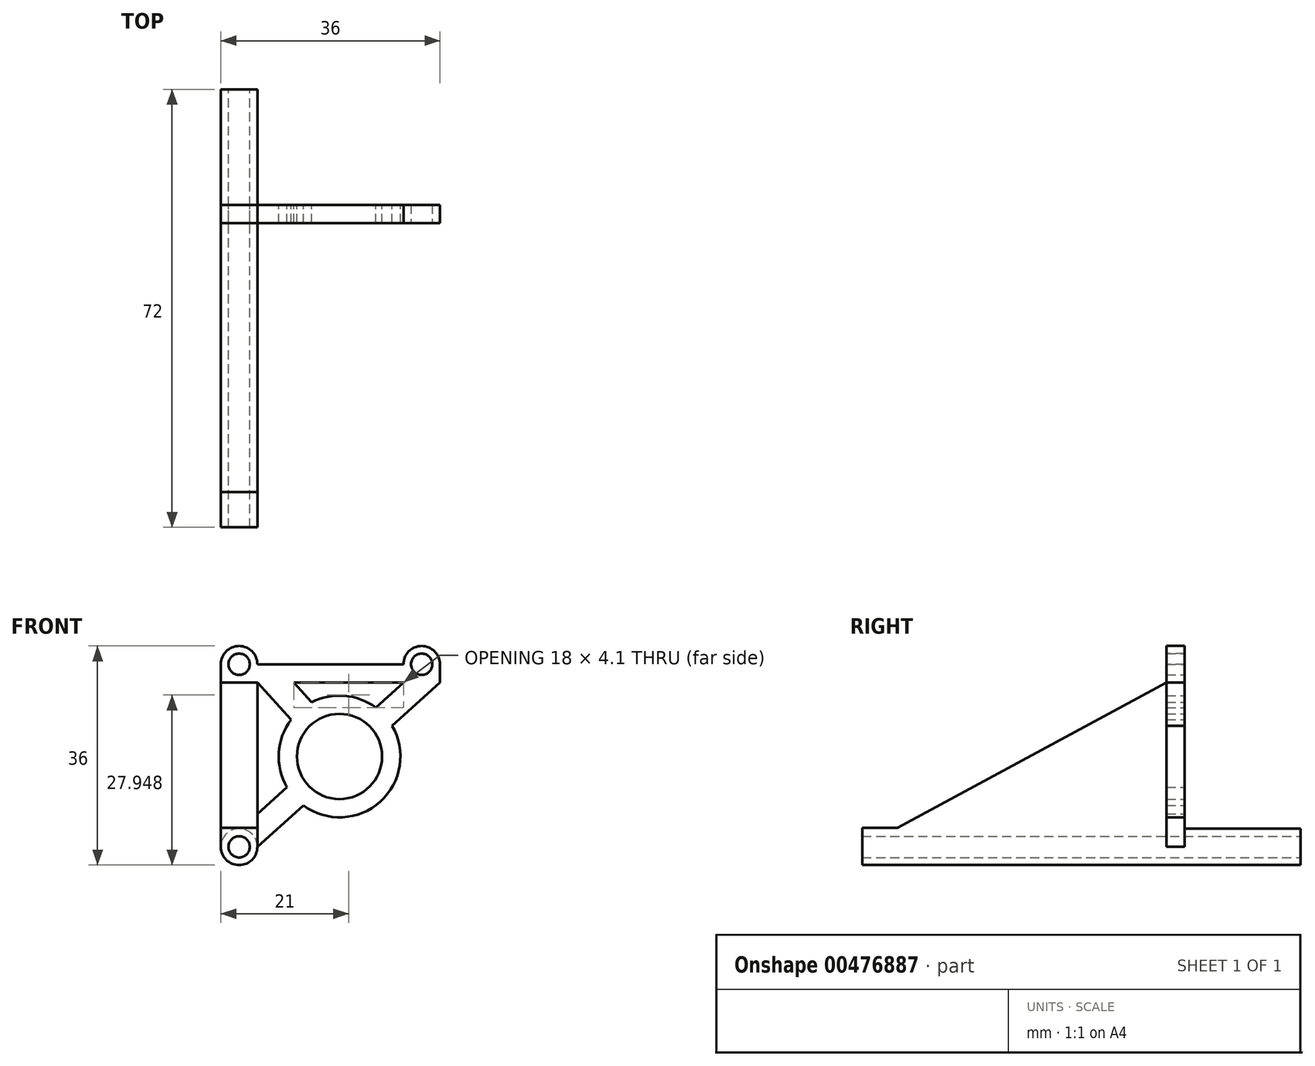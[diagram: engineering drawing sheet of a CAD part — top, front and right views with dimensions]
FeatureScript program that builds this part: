
annotation { "Feature Type Name" : "Feature", "Feature Type Description" : "" }
export const myFeature = defineFeature(function(context is Context, id is Id, definition is map)
    precondition{}
    {
        {
            var Q0;
            Q0=qCreatedBy(makeId("Front.planeOp"),FACE);
            var sketch = newSketch(context, id + "F0", { "sketchPlane" : qUnion([Q0])});
            skCircle(sketch, "E0", {"center": v(0, 0) * mm, "radius": 1.75 * mm});
            skCircle(sketch, "E1", {"center": v(0, 0) * mm, "radius": 3 * mm});
            skSolve(sketch);
        }
        {
            var Q0;
            Q0 = qSketchRegion(id + "F0", true);
            extrude(context, id + "F1", {"entities" : qUnion([Q0]), "depth" : 16 * mm, "hasSecondDirection" : true, "secondDirectionOppositeDirection" : true, "secondDirectionDepth" : 3 * mm});
        }
        {
            var Q0;
            Q0=makeQuery(id+"F1.opExtrude","CAP_FACE",FACE,{"disambiguationData":[OSD([sQuery(id+"F0.wireOp",EDGE,"E0"),sQuery(id+"F0.wireOp",EDGE,"E1")])],"isStart":false});
            var sketch = newSketch(context, id + "F2", { "sketchPlane" : qUnion([Q0])});
            skLineSegment(sketch, "E2", {"start": v(-3, 0) * mm, "end": v(-3, 30) * mm});
            skLineSegment(sketch, "E3", {"start": v(3, 0) * mm, "end": v(3, 30) * mm});
            skArc(sketch, "E4", {"start": v(-3, 0) * mm, "mid": v(0, -3) * mm, "end": v(3, 0) * mm});
            skArc(sketch, "E5", {"start": v(3, 30) * mm, "mid": v(0, 33) * mm, "end": v(-3, 30) * mm});
            skLineSegment(sketch, "E6", {"start": v(-3, 30) * mm, "end": v(3, 30) * mm, "construction": true});
            skCircle(sketch, "E7", {"center": v(0, 30) * mm, "radius": 1.75 * mm});
            skSolve(sketch);
        }
        {
            var Q0;
            Q0 = qSketchRegion(id + "F2", true);
            extrude(context, id + "F3", {"entities" : qUnion([Q0]), "operationType" : NewBodyOperationType.ADD, "depth" : 3 * mm});
        }
        {
            var Q0;
            Q0=makeQuery(id+"F3.opExtrude","SWEPT_FACE",FACE,{"disambiguationData":[OSD([sQuery(id+"F2.wireOp",EDGE,"E2")])]});
            var sketch = newSketch(context, id + "F4", { "sketchPlane" : qUnion([Q0])});
            skLineSegment(sketch, "E8", {"start": v(19, 27) * mm, "end": v(69, 0) * mm});
            skLineSegment(sketch, "E9", {"start": v(69, 0) * mm, "end": v(19, 0) * mm});
            skSolve(sketch);
        }
        {
            var Q0;
            {var subQ0=sQuery(id+"F4.wireOp",EDGE,"E8");Q0=makeQuery(id+"F4.imprint","IMPRINT",FACE,{"disambiguationData":[TD([[makeQuery(id+"F4.imprint","IMPRINT",EDGE,{"derivedFrom":subQ0}),-1.0]])]});}
            var Q1;
            Q1=makeQuery(id+"F3.opExtrude","SWEPT_FACE",FACE,{"disambiguationData":[OSD([sQuery(id+"F2.wireOp",EDGE,"E3")])]});
            extrude(context, id + "F5", {"entities" : qUnion([Q0]), "operationType" : NewBodyOperationType.ADD, "endBound" : BoundingType.UP_TO_SURFACE, "oppositeDirection" : true, "endBoundEntityFace" : qUnion([Q1]), "depth" : 5 * mm});
        }
        {
            var Q0;
            {var subQ0=sQuery(id+"F2.wireOp",EDGE,"E4");var subQ1=sQuery(id+"F2.wireOp",EDGE,"E3");var subQ2=sQuery(id+"F2.wireOp",EDGE,"E2");Q0=makeQuery(id+"F5.boolean.opBoolean","SPLIT",FACE,{"disambiguationData":[TD([makeQuery(id+"F1.opExtrude","SWEPT_FACE",FACE,{"disambiguationData":[OSD([sQuery(id+"F0.wireOp",EDGE,"E1")])]})])],"derivedFrom":makeQuery(id+"F3.opExtrude","CAP_FACE",FACE,{"disambiguationData":[OSD([subQ2,subQ1,subQ0,sQuery(id+"F2.wireOp",EDGE,"E5"),sQuery(id+"F2.wireOp",EDGE,"E7")])],"isStart":false})});}
            var sketch = newSketch(context, id + "F6", { "sketchPlane" : qUnion([Q0])});
            skArc(sketch, "E10", {"start": v(-3, 0) * mm, "mid": v(0, -3) * mm, "end": v(3, 0) * mm});
            skLineSegment(sketch, "E11", {"start": v(-3, 0) * mm, "end": v(3, 0) * mm});
            skSolve(sketch);
        }
        {
            var Q0;
            Q0 = qSketchRegion(id + "F6", true);
            var Q1;
            Q1=makeQuery(id+"F5.opExtrude","CAP_VERTEX",VERTEX,{"disambiguationData":[OSD([sQuery(id+"F4.wireOp",EDGE,"E8"),sQuery(id+"F4.wireOp",EDGE,"E9")])],"isStart":true});
            extrude(context, id + "F7", {"entities" : qUnion([Q0]), "operationType" : NewBodyOperationType.ADD, "endBound" : BoundingType.UP_TO_VERTEX, "endBoundEntityVertex" : qUnion([Q1]), "depth" : 25.4 * mm});
        }
        {
            var Q0;
            Q0=makeQuery(id+"F1.opExtrude","CAP_FACE",FACE,{"disambiguationData":[OSD([sQuery(id+"F0.wireOp",EDGE,"E0"),sQuery(id+"F0.wireOp",EDGE,"E1")])],"isStart":true});
            var sketch = newSketch(context, id + "F8", { "sketchPlane" : qUnion([Q0])});
            skCircle(sketch, "E12", {"center": v(0, 0) * mm, "radius": 1.75 * mm});
            skSolve(sketch);
        }
        {
            var Q0;
            Q0=makeQuery(id+"F7.opExtrude","CAP_FACE",FACE,{"disambiguationData":[OSD([sQuery(id+"F6.wireOp",EDGE,"E10"),sQuery(id+"F6.wireOp",EDGE,"E11")])],"isStart":false});
            var sketch = newSketch(context, id + "F9", { "sketchPlane" : qUnion([Q0])});
            skArc(sketch, "E13", {"start": v(-3, 0) * mm, "mid": v(0, -3) * mm, "end": v(3, 0) * mm});
            skLineSegment(sketch, "E14.top", {"start": v(-3, 3.13) * mm, "end": v(3, 3.13) * mm});
            skLineSegment(sketch, "E14.left", {"start": v(-3, 0) * mm, "end": v(-3, 3.13) * mm});
            skLineSegment(sketch, "E14.right", {"start": v(3, 0) * mm, "end": v(3, 3.13) * mm});
            skSolve(sketch);
        }
        {
            var Q0;
            Q0 = qSketchRegion(id + "F9", true);
            extrude(context, id + "F10", {"entities" : qUnion([Q0]), "operationType" : NewBodyOperationType.ADD, "oppositeDirection" : true, "depth" : 6 * mm});
        }
        {
            var Q0;
            Q0 = qSketchRegion(id + "F8", true);
            extrude(context, id + "F11", {"entities" : qUnion([Q0]), "operationType" : NewBodyOperationType.REMOVE, "endBound" : BoundingType.THROUGH_ALL, "oppositeDirection" : true, "depth" : 25.4 * mm});
        }
        {
            var Q0;
            {var subQ0=sQuery(id+"F2.wireOp",EDGE,"E7");var subQ3=sQuery(id+"F2.wireOp",EDGE,"E2");var subQ4=sQuery(id+"F2.wireOp",EDGE,"E3");var subQ5=sQuery(id+"F2.wireOp",EDGE,"E5");Q0=makeQuery(id+"F5.boolean.opBoolean","SPLIT",FACE,{"disambiguationData":[TD([makeQuery(id+"F3.opExtrude","SWEPT_FACE",FACE,{"disambiguationData":[OSD([subQ5])]})])],"derivedFrom":makeQuery(id+"F3.opExtrude","CAP_FACE",FACE,{"disambiguationData":[OSD([subQ3,subQ4,sQuery(id+"F2.wireOp",EDGE,"E4"),subQ5,subQ0])],"isStart":false})});}
            var sketch = newSketch(context, id + "F12", { "sketchPlane" : qUnion([Q0])});
            skCircle(sketch, "E15", {"center": v(30, 30) * mm, "radius": 1.75 * mm});
            skLineSegment(sketch, "E16", {"start": v(0, 30) * mm, "end": v(30, 30) * mm, "construction": true});
            skArc(sketch, "E17", {"start": v(33, 30) * mm, "mid": v(30, 33) * mm, "end": v(27, 30) * mm});
            skLineSegment(sketch, "E18", {"start": v(27, 30) * mm, "end": v(27, 27) * mm});
            skLineSegment(sketch, "E19", {"start": v(27, 27) * mm, "end": v(33, 27) * mm});
            skLineSegment(sketch, "E20", {"start": v(33, 27) * mm, "end": v(33, 30) * mm});
            skSolve(sketch);
        }
        {
            var Q0;
            Q0 = qSketchRegion(id + "F12", true);
            extrude(context, id + "F13", {"entities" : qUnion([Q0]), "oppositeDirection" : true, "depth" : 3 * mm});
        }
        {
            var Q0;
            Q0=makeQuery(id+"F10.boolean.opBoolean","MERGE",FACE,{"derivedFrom":[makeQuery(id+"F5.boolean.opBoolean","MERGE",FACE,{"derivedFrom":[makeQuery(id+"F3.opExtrude","SWEPT_FACE",FACE,{"disambiguationData":[OSD([sQuery(id+"F2.wireOp",EDGE,"E3")])]}),makeQuery(id+"F5.opExtrude","CAP_FACE",FACE,{"disambiguationData":[OSD([sQuery(id+"F2.wireOp",EDGE,"E2"),sQuery(id+"F4.wireOp",EDGE,"E8"),sQuery(id+"F4.wireOp",EDGE,"E9")])],"isStart":false})]}),makeQuery(id+"F10.opExtrude","SWEPT_FACE",FACE,{"disambiguationData":[OSD([sQuery(id+"F9.wireOp",EDGE,"E14.right")])]})]});
            var sketch = newSketch(context, id + "F14", { "sketchPlane" : qUnion([Q0])});
            skLineSegment(sketch, "E21.bottom", {"start": v(-19, 30) * mm, "end": v(-16, 30) * mm});
            skLineSegment(sketch, "E21.top", {"start": v(-19, 27) * mm, "end": v(-16, 27) * mm});
            skLineSegment(sketch, "E21.left", {"start": v(-19, 30) * mm, "end": v(-19, 27) * mm});
            skLineSegment(sketch, "E21.right", {"start": v(-16, 30) * mm, "end": v(-16, 27) * mm});
            skSolve(sketch);
        }
        {
            var Q0;
            Q0 = qSketchRegion(id + "F14", true);
            var Q1;
            Q1=makeQuery(id+"F13.opExtrude","SWEPT_FACE",FACE,{"disambiguationData":[OSD([sQuery(id+"F12.wireOp",EDGE,"E18")])]});
            extrude(context, id + "F15", {"entities" : qUnion([Q0]), "operationType" : NewBodyOperationType.ADD, "endBound" : BoundingType.UP_TO_SURFACE, "endBoundEntityFace" : qUnion([Q1]), "depth" : 25.4 * mm});
        }
        {
            var Q0;
            {var subQ0=sQuery(id+"F2.wireOp",EDGE,"E4");var subQ1=sQuery(id+"F2.wireOp",EDGE,"E3");var subQ2=sQuery(id+"F2.wireOp",EDGE,"E2");var subQ3=sQuery(id+"F2.wireOp",EDGE,"E5");var subQ4=sQuery(id+"F2.wireOp",EDGE,"E7");Q0=makeQuery(id+"F15.boolean.opBoolean","MERGE",FACE,{"derivedFrom":[makeQuery(id+"F3.boolean.opBoolean","SPLIT",FACE,{"disambiguationData":[TD([makeQuery(id+"F1.opExtrude","SWEPT_FACE",FACE,{"disambiguationData":[OSD([sQuery(id+"F0.wireOp",EDGE,"E1")])]})])],"derivedFrom":makeQuery(id+"F3.opExtrude","CAP_FACE",FACE,{"disambiguationData":[OSD([subQ2,subQ1,subQ0,subQ3,subQ4])],"isStart":true})}),makeQuery(id+"F15.opExtrude","SWEPT_FACE",FACE,{"disambiguationData":[OSD([sQuery(id+"F14.wireOp",EDGE,"E21.right")])]})]});}
            var sketch = newSketch(context, id + "F16", { "sketchPlane" : qUnion([Q0])});
            skLineSegment(sketch, "E22", {"start": v(-33, 27) * mm, "end": v(-3, 0) * mm});
            skLineSegment(sketch, "E23", {"start": v(-27, 27) * mm, "end": v(-3, 5.4) * mm});
            skLineSegment(sketch, "E24", {"start": v(-33, 27) * mm, "end": v(-27, 27) * mm});
            skLineSegment(sketch, "E25", {"start": v(-3, 5.4) * mm, "end": v(-3, 0) * mm});
            skSolve(sketch);
        }
        {
            var Q0;
            Q0 = qSketchRegion(id + "F16", true);
            var Q1;
            {var subQ0=sQuery(id+"F2.wireOp",EDGE,"E7");var subQ3=sQuery(id+"F2.wireOp",EDGE,"E2");var subQ4=sQuery(id+"F2.wireOp",EDGE,"E3");var subQ5=sQuery(id+"F2.wireOp",EDGE,"E5");Q1=makeQuery(id+"F15.boolean.opBoolean","MERGE",FACE,{"derivedFrom":[makeQuery(id+"F5.boolean.opBoolean","SPLIT",FACE,{"disambiguationData":[TD([makeQuery(id+"F3.opExtrude","SWEPT_FACE",FACE,{"disambiguationData":[OSD([subQ5])]})])],"derivedFrom":makeQuery(id+"F3.opExtrude","CAP_FACE",FACE,{"disambiguationData":[OSD([subQ3,subQ4,sQuery(id+"F2.wireOp",EDGE,"E4"),subQ5,subQ0])],"isStart":false})}),makeQuery(id+"F13.opExtrude","CAP_FACE",FACE,{"disambiguationData":[OSD([sQuery(id+"F12.wireOp",EDGE,"E15"),sQuery(id+"F12.wireOp",EDGE,"E17"),sQuery(id+"F12.wireOp",EDGE,"E18"),sQuery(id+"F12.wireOp",EDGE,"E19"),sQuery(id+"F12.wireOp",EDGE,"E20")])],"isStart":true}),makeQuery(id+"F15.opExtrude","SWEPT_FACE",FACE,{"disambiguationData":[OSD([sQuery(id+"F14.wireOp",EDGE,"E21.left")])]})]});}
            extrude(context, id + "F17", {"entities" : qUnion([Q0]), "operationType" : NewBodyOperationType.ADD, "endBound" : BoundingType.UP_TO_SURFACE, "oppositeDirection" : true, "endBoundEntityFace" : qUnion([Q1]), "depth" : 25.4 * mm});
        }
        {
            var Q0;
            {var subQ0=sQuery(id+"F2.wireOp",EDGE,"E4");var subQ1=sQuery(id+"F2.wireOp",EDGE,"E3");var subQ2=sQuery(id+"F2.wireOp",EDGE,"E2");var subQ3=sQuery(id+"F2.wireOp",EDGE,"E5");var subQ4=sQuery(id+"F2.wireOp",EDGE,"E7");Q0=makeQuery(id+"F17.boolean.opBoolean","MERGE",FACE,{"derivedFrom":[makeQuery(id+"F15.boolean.opBoolean","MERGE",FACE,{"derivedFrom":[makeQuery(id+"F3.boolean.opBoolean","SPLIT",FACE,{"disambiguationData":[TD([makeQuery(id+"F1.opExtrude","SWEPT_FACE",FACE,{"disambiguationData":[OSD([sQuery(id+"F0.wireOp",EDGE,"E1")])]})])],"derivedFrom":makeQuery(id+"F3.opExtrude","CAP_FACE",FACE,{"disambiguationData":[OSD([subQ2,subQ1,subQ0,subQ3,subQ4])],"isStart":true})}),makeQuery(id+"F15.opExtrude","SWEPT_FACE",FACE,{"disambiguationData":[OSD([sQuery(id+"F14.wireOp",EDGE,"E21.right")])]})]}),makeQuery(id+"F17.opExtrude","CAP_FACE",FACE,{"disambiguationData":[OSD([sQuery(id+"F16.wireOp",EDGE,"E22"),sQuery(id+"F16.wireOp",EDGE,"E23"),sQuery(id+"F16.wireOp",EDGE,"E24"),sQuery(id+"F16.wireOp",EDGE,"E25")])],"isStart":true})]});}
            var sketch = newSketch(context, id + "F18", { "sketchPlane" : qUnion([Q0])});
            skCircle(sketch, "E26", {"center": v(-16.5, 14.85) * mm, "radius": 10 * mm});
            skLineSegment(sketch, "E27", {"start": v(-30, 27) * mm, "end": v(-3, 2.7) * mm, "construction": true});
            skLineSegment(sketch, "E28", {"start": v(-33, 27) * mm, "end": v(-27, 27) * mm, "construction": true});
            skLineSegment(sketch, "E29", {"start": v(-3, 5.4) * mm, "end": v(-3, 0) * mm, "construction": true});
            skCircle(sketch, "E30", {"center": v(-16.5, 14.85) * mm, "radius": 7 * mm});
            skSolve(sketch);
        }
        {
            var Q0;
            Q0 = qSketchRegion(id + "F18", true);
            var Q1;
            {var subQ0=sQuery(id+"F2.wireOp",EDGE,"E7");var subQ3=sQuery(id+"F2.wireOp",EDGE,"E2");var subQ4=sQuery(id+"F2.wireOp",EDGE,"E3");var subQ5=sQuery(id+"F2.wireOp",EDGE,"E5");Q1=makeQuery(id+"F17.boolean.opBoolean","MERGE",FACE,{"derivedFrom":[makeQuery(id+"F15.boolean.opBoolean","MERGE",FACE,{"derivedFrom":[makeQuery(id+"F5.boolean.opBoolean","SPLIT",FACE,{"disambiguationData":[TD([makeQuery(id+"F3.opExtrude","SWEPT_FACE",FACE,{"disambiguationData":[OSD([subQ5])]})])],"derivedFrom":makeQuery(id+"F3.opExtrude","CAP_FACE",FACE,{"disambiguationData":[OSD([subQ3,subQ4,sQuery(id+"F2.wireOp",EDGE,"E4"),subQ5,subQ0])],"isStart":false})}),makeQuery(id+"F13.opExtrude","CAP_FACE",FACE,{"disambiguationData":[OSD([sQuery(id+"F12.wireOp",EDGE,"E15"),sQuery(id+"F12.wireOp",EDGE,"E17"),sQuery(id+"F12.wireOp",EDGE,"E18"),sQuery(id+"F12.wireOp",EDGE,"E19"),sQuery(id+"F12.wireOp",EDGE,"E20")])],"isStart":true}),makeQuery(id+"F15.opExtrude","SWEPT_FACE",FACE,{"disambiguationData":[OSD([sQuery(id+"F14.wireOp",EDGE,"E21.left")])]})]}),makeQuery(id+"F17.opExtrude","CAP_FACE",FACE,{"disambiguationData":[OSD([sQuery(id+"F16.wireOp",EDGE,"E22"),sQuery(id+"F16.wireOp",EDGE,"E23"),sQuery(id+"F16.wireOp",EDGE,"E24"),sQuery(id+"F16.wireOp",EDGE,"E25")])],"isStart":false})]});}
            extrude(context, id + "F19", {"entities" : qUnion([Q0]), "operationType" : NewBodyOperationType.ADD, "endBound" : BoundingType.UP_TO_SURFACE, "oppositeDirection" : true, "endBoundEntityFace" : qUnion([Q1]), "depth" : 25.4 * mm});
        }
        {
            var Q0;
            {var subQ0=sQuery(id+"F2.wireOp",EDGE,"E4");var subQ1=sQuery(id+"F2.wireOp",EDGE,"E3");var subQ2=sQuery(id+"F2.wireOp",EDGE,"E2");var subQ3=sQuery(id+"F2.wireOp",EDGE,"E5");var subQ4=sQuery(id+"F2.wireOp",EDGE,"E7");Q0=makeQuery(id+"F19.boolean.opBoolean","MERGE",FACE,{"derivedFrom":[makeQuery(id+"F17.boolean.opBoolean","MERGE",FACE,{"derivedFrom":[makeQuery(id+"F15.boolean.opBoolean","MERGE",FACE,{"derivedFrom":[makeQuery(id+"F3.boolean.opBoolean","SPLIT",FACE,{"disambiguationData":[TD([makeQuery(id+"F1.opExtrude","SWEPT_FACE",FACE,{"disambiguationData":[OSD([sQuery(id+"F0.wireOp",EDGE,"E1")])]})])],"derivedFrom":makeQuery(id+"F3.opExtrude","CAP_FACE",FACE,{"disambiguationData":[OSD([subQ2,subQ1,subQ0,subQ3,subQ4])],"isStart":true})}),makeQuery(id+"F15.opExtrude","SWEPT_FACE",FACE,{"disambiguationData":[OSD([sQuery(id+"F14.wireOp",EDGE,"E21.right")])]})]}),makeQuery(id+"F17.opExtrude","CAP_FACE",FACE,{"disambiguationData":[OSD([sQuery(id+"F16.wireOp",EDGE,"E22"),sQuery(id+"F16.wireOp",EDGE,"E23"),sQuery(id+"F16.wireOp",EDGE,"E24"),sQuery(id+"F16.wireOp",EDGE,"E25")])],"isStart":true})]}),makeQuery(id+"F19.opExtrude","CAP_FACE",FACE,{"disambiguationData":[OSD([sQuery(id+"F18.wireOp",EDGE,"E26"),sQuery(id+"F18.wireOp",EDGE,"E30")])],"isStart":true})]});}
            var sketch = newSketch(context, id + "F20", { "sketchPlane" : qUnion([Q0])});
            skLineSegment(sketch, "E31", {"start": v(-3, 27) * mm, "end": v(-10.5, 18.66) * mm});
            skLineSegment(sketch, "E32", {"start": v(-14.04, 21.4) * mm, "end": v(-9, 27) * mm});
            skLineSegment(sketch, "E33", {"start": v(-9, 27) * mm, "end": v(-3, 27) * mm, "construction": true});
            skLineSegment(sketch, "E34", {"start": v(-20.14, 20.83) * mm, "end": v(-10.17, 11.86) * mm, "construction": true});
            skLineSegment(sketch, "E35", {"start": v(-6, 27) * mm, "end": v(-15.4, 16.56) * mm, "construction": true});
            skSolve(sketch);
        }
        {
            var Q0;
            Q0 = qSketchRegion(id + "F20", true);
            var Q1;
            {var subQ1=sQuery(id+"F2.wireOp",EDGE,"E3");var subQ2=sQuery(id+"F14.wireOp",EDGE,"E21.right");var subQ3=makeQuery(id+"F15.opExtrude","SWEPT_EDGE",EDGE,{"disambiguationData":[OSD([subQ1,sQuery(id+"F14.wireOp",EDGE,"E21.top"),subQ2])]});var subQ9=sQuery(id+"F20.wireOp",EDGE,"E32");var subQ10=makeQuery(id+"F20.imprint","INTERSECT",VERTEX,{"derivedFrom":[subQ3,subQ9]});Q1=makeQuery(id+"F20.imprint","IMPRINT",FACE,{"disambiguationData":[TD([[makeQuery(id+"F20.imprint","IMPRINT",EDGE,{"disambiguationData":[TD([[subQ10,-1.0]])],"derivedFrom":subQ3}),-1.0]])]});}
            var Q2;
            {var subQ0=sQuery(id+"F2.wireOp",EDGE,"E7");var subQ3=sQuery(id+"F2.wireOp",EDGE,"E2");var subQ4=sQuery(id+"F2.wireOp",EDGE,"E3");var subQ5=sQuery(id+"F2.wireOp",EDGE,"E5");Q2=makeQuery(id+"F19.boolean.opBoolean","MERGE",FACE,{"derivedFrom":[makeQuery(id+"F17.boolean.opBoolean","MERGE",FACE,{"derivedFrom":[makeQuery(id+"F15.boolean.opBoolean","MERGE",FACE,{"derivedFrom":[makeQuery(id+"F5.boolean.opBoolean","SPLIT",FACE,{"disambiguationData":[TD([makeQuery(id+"F3.opExtrude","SWEPT_FACE",FACE,{"disambiguationData":[OSD([subQ5])]})])],"derivedFrom":makeQuery(id+"F3.opExtrude","CAP_FACE",FACE,{"disambiguationData":[OSD([subQ3,subQ4,sQuery(id+"F2.wireOp",EDGE,"E4"),subQ5,subQ0])],"isStart":false})}),makeQuery(id+"F13.opExtrude","CAP_FACE",FACE,{"disambiguationData":[OSD([sQuery(id+"F12.wireOp",EDGE,"E15"),sQuery(id+"F12.wireOp",EDGE,"E17"),sQuery(id+"F12.wireOp",EDGE,"E18"),sQuery(id+"F12.wireOp",EDGE,"E19"),sQuery(id+"F12.wireOp",EDGE,"E20")])],"isStart":true}),makeQuery(id+"F15.opExtrude","SWEPT_FACE",FACE,{"disambiguationData":[OSD([sQuery(id+"F14.wireOp",EDGE,"E21.left")])]})]}),makeQuery(id+"F17.opExtrude","CAP_FACE",FACE,{"disambiguationData":[OSD([sQuery(id+"F16.wireOp",EDGE,"E22"),sQuery(id+"F16.wireOp",EDGE,"E23"),sQuery(id+"F16.wireOp",EDGE,"E24"),sQuery(id+"F16.wireOp",EDGE,"E25")])],"isStart":false})]}),makeQuery(id+"F19.opExtrude","CAP_FACE",FACE,{"disambiguationData":[OSD([sQuery(id+"F18.wireOp",EDGE,"E26"),sQuery(id+"F18.wireOp",EDGE,"E30")])],"isStart":false})]});}
            extrude(context, id + "F21", {"entities" : qUnion([Q0, Q1]), "operationType" : NewBodyOperationType.ADD, "endBound" : BoundingType.UP_TO_SURFACE, "oppositeDirection" : true, "endBoundEntityFace" : qUnion([Q2]), "depth" : 25.4 * mm});
        }
        {
            var Q0;
            {var subQ0=sQuery(id+"F18.wireOp",EDGE,"E26");var subQ1=sQuery(id+"F14.wireOp",EDGE,"E21.right");var subQ2=sQuery(id+"F2.wireOp",EDGE,"E3");var subQ3=sQuery(id+"F2.wireOp",EDGE,"E4");var subQ4=sQuery(id+"F2.wireOp",EDGE,"E2");var subQ5=sQuery(id+"F2.wireOp",EDGE,"E5");var subQ6=sQuery(id+"F2.wireOp",EDGE,"E7");Q0=makeQuery(id+"F21.boolean.opBoolean","MERGE",FACE,{"derivedFrom":[makeQuery(id+"F19.boolean.opBoolean","MERGE",FACE,{"derivedFrom":[makeQuery(id+"F17.boolean.opBoolean","MERGE",FACE,{"derivedFrom":[makeQuery(id+"F15.boolean.opBoolean","MERGE",FACE,{"derivedFrom":[makeQuery(id+"F3.boolean.opBoolean","SPLIT",FACE,{"disambiguationData":[TD([makeQuery(id+"F1.opExtrude","SWEPT_FACE",FACE,{"disambiguationData":[OSD([sQuery(id+"F0.wireOp",EDGE,"E1")])]})])],"derivedFrom":makeQuery(id+"F3.opExtrude","CAP_FACE",FACE,{"disambiguationData":[OSD([subQ4,subQ2,subQ3,subQ5,subQ6])],"isStart":true})}),makeQuery(id+"F15.opExtrude","SWEPT_FACE",FACE,{"disambiguationData":[OSD([subQ1])]})]}),makeQuery(id+"F17.opExtrude","CAP_FACE",FACE,{"disambiguationData":[OSD([sQuery(id+"F16.wireOp",EDGE,"E22"),sQuery(id+"F16.wireOp",EDGE,"E23"),sQuery(id+"F16.wireOp",EDGE,"E24"),sQuery(id+"F16.wireOp",EDGE,"E25")])],"isStart":true})]}),makeQuery(id+"F19.opExtrude","CAP_FACE",FACE,{"disambiguationData":[OSD([subQ0,sQuery(id+"F18.wireOp",EDGE,"E30")])],"isStart":true})]}),makeQuery(id+"F21.opExtrude","CAP_FACE",FACE,{"disambiguationData":[OSD([subQ2,sQuery(id+"F14.wireOp",EDGE,"E21.top"),subQ1,subQ0,sQuery(id+"F20.wireOp",EDGE,"E31"),sQuery(id+"F20.wireOp",EDGE,"E32")])],"isStart":true})]});}
            var sketch = newSketch(context, id + "F22", { "sketchPlane" : qUnion([Q0])});
            skCircle(sketch, "E36", {"center": v(-16.5, 14.85) * mm, "radius": 7 * mm});
            skSolve(sketch);
        }
        {
            var Q0;
            Q0 = qSketchRegion(id + "F22", true);
            extrude(context, id + "F23", {"entities" : qUnion([Q0]), "operationType" : NewBodyOperationType.REMOVE, "oppositeDirection" : true, "depth" : 25.4 * mm});
        }
    });
